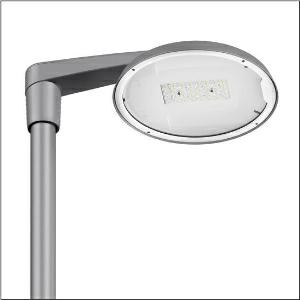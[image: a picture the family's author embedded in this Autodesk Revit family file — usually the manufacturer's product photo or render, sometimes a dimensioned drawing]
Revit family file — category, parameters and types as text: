
# Revit family: dl_50_iq_mini___st0_5a_5xa248b31f08fe_8559
name_source: partatom
category: Lighting Fixtures
units: mm (PartAtom-declared; Revit-internal decimal feet)

## family parameters
Cut with Voids When Loaded = No
Host = Face
Light Source = No
Part Type = Normal
Room Calculation Point = No
Round Connector Dimension = Use Diameter
Shared = No

## types (1)
- --- (1 x LED, 2700 lm, 16.3 W, 3000K)
    Apparent Load = 16 VA
    CIE Flux Codes = 41 75 97 100 100
    Color Rendering = 70
    Color Temperature = 3000K
    Default Elevation = 1800 mm
    Description = DL 50 iQ mini, mast luminaire, primary light control with lens, of PMMA, primary optical cover: cover, of toughened safety glass, transparent, light distribution: ST0.5a, light emission: direct distribution, primary light characteristic: asymmetric, installation type: side-entry, post-top, LED, High Power LED, rated luminous flux: 2.700lm, luminous efficacy: 166lm/W, light colour: 730, colour temperature: 3000K, control gear: iQ Street-Remote, control: optimised constant luminous flux control (CLO 2.0), Desk-Remote (wireless, voltage-free reading and setting of iQ features in the workshop via application-optimized NFC function/RFID function), Light-Fading, Smart-Wire, Night-Set, Lumen-Switch, Temp-Guard, Auto-Match, Street-Remote, mains connection: 230..240V, AC, 50/60Hz, connection cable pre-assembled, cable length: 6,5m, start of lifetime: 16W, end of service life: 17W, reduction: 8W, luminaire housing, of diecast aluminium, powder-coated, SITECO metallic grey (DB 702S), inclination adjustable: 0°, 5°, 10° (post-top) | 0°, -5°, -10°, -15° (side-entry), please order mast post-top element or mast side-entry element separately, diameter: 500mm, height: 115mm, post-top: for spigot size d x l = 76 x 100mm; with reducer (optional accessory) 60 x 100mm | side-entry: for spigot size d x l = 60 x 100mm; with reducer (optional accessory) 42 x 100mm, mounting height: 4..6m, protection rating (complete): IP66, insulation class (complete): insulation class II (safety insulation), certification: CE, ENEC, ENEC+, VDE, impact resistance: IK08, permissible operating ambient temperature for outdoor applications: -25..+40°C, standard-compliant lighting for roads and squares, packaging unit: 1 piece

Light Distribution: ST0.5a
    Height = 115 mm
    Lamp = 1 x LED
    Lamp Light Flux = 2700 lm
    Lamp Power = 16.3 W
    Lamp count = 1
    Length = 500 mm
    Luminous efficacy = 166 lm/W
    Manufacturer = Siteco
    ModVariant = No
    Model = 5XA248B31F08FE
    Mounting Place = Pole
    Mounting Type = Pole top
    Number of Poles = 1
    OnlyDefault = Yes
    Power Factor = 1
    Product Name = DL 50 iQ mini | ST0.5a
    Product group = mast luminaire | pylon top
    ProductGroupID = 6100
    Protection Class = Protection class II
    Protection Degree = IP 66
    RLX_Detail_Level = 1
    RLX_Emergency_Light_Flux = 0 lm
    RLX_Emergency_Type = 0
    RLX_Emergency_Type_DB = No
    RlxData = <blob elided: 126657 chars, md5=c8d23866>
    Socket = socket
    Standby Power = 0 W
    System Light Flux = 2700 lm
    System Power = 16 W
    Type Comments = factory setting: luminous flux: 100 % | dim-lin: 254 | 333 mA
    Type Image = l_1251794.jpg
    URL = http://relux.com
    VarID = @adj_140481
    Voltage = 0 V
    Weight = 0.00 kg
    Width = 0 mm  [stored 0 ft]

note: [stored X ft] marks values corroborated as IEEE doubles in the binary element streams (Revit-internal decimal feet)

## geometry (parser evidence)
native form markers: Blend x4, Sweep x11
no freeform markers — native parametric forms only
